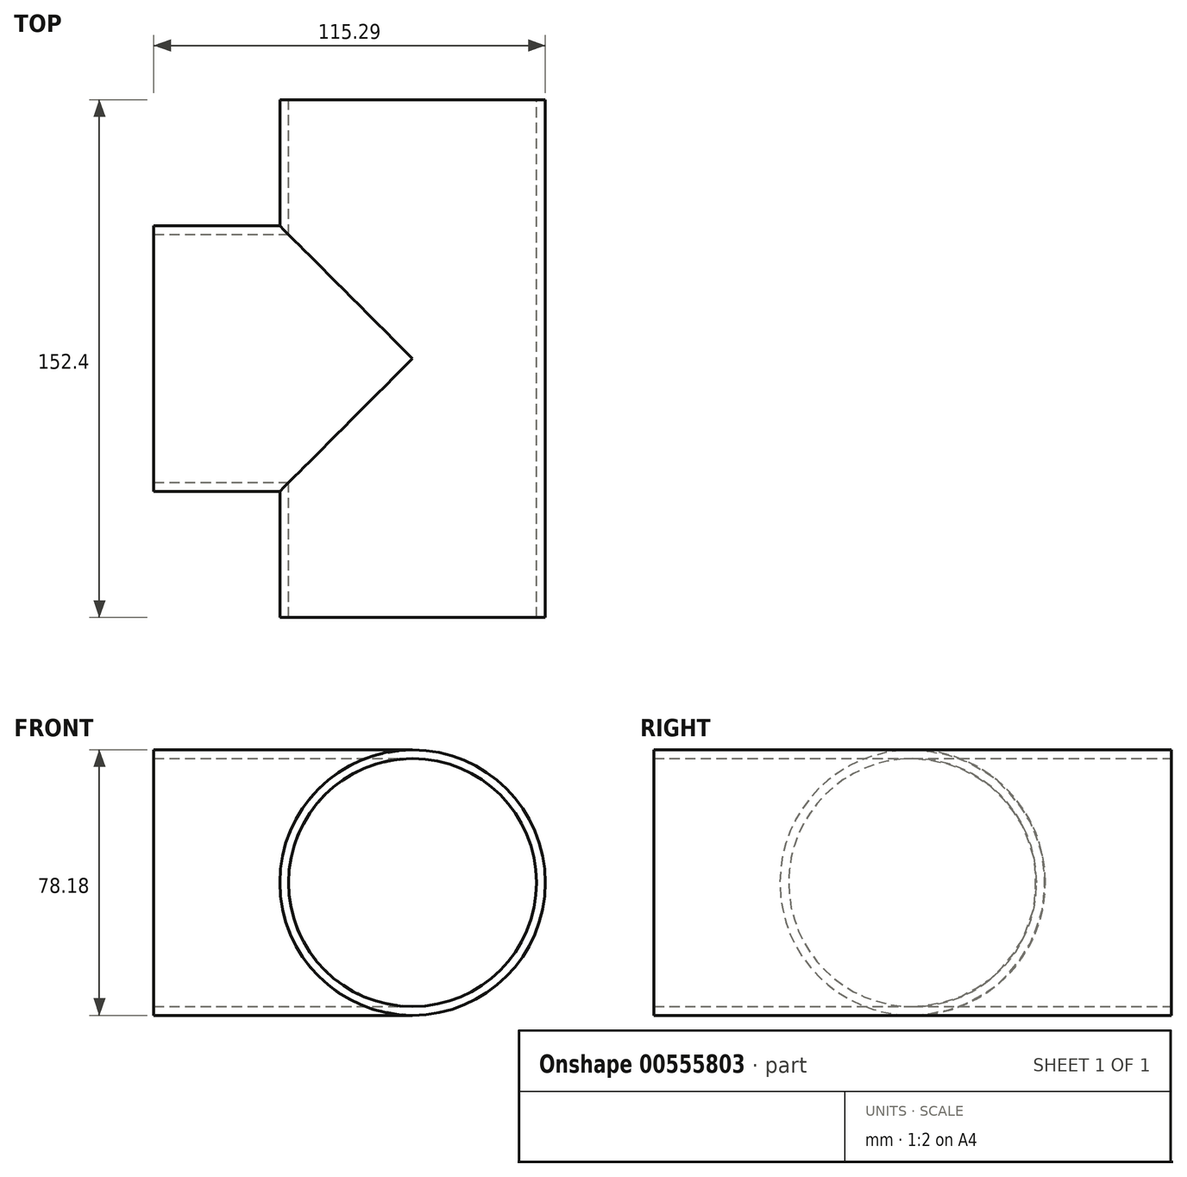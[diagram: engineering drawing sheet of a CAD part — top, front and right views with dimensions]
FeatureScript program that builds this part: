
annotation { "Feature Type Name" : "Feature", "Feature Type Description" : "" }
export const myFeature = defineFeature(function(context is Context, id is Id, definition is map)
    precondition{}
    {
        {
            var Q0;
            Q0=qCreatedBy(makeId("Front.planeOp"),FACE);
            var sketch = newSketch(context, id + "F0", { "sketchPlane" : qUnion([Q0])});
            skCircle(sketch, "E0", {"center": v(0, 0) * mm, "radius": 36.51 * mm});
            skCircle(sketch, "E1", {"center": v(0, 0) * mm, "radius": 39.1 * mm});
            skSolve(sketch);
        }
        {
            var Q0;
            Q0=qCreatedBy(makeId("Right.planeOp"),FACE);
            var sketch = newSketch(context, id + "F1", { "sketchPlane" : qUnion([Q0])});
            skLineSegment(sketch, "E2", {"start": v(0, 0) * mm, "end": v(152.4, 0) * mm});
            skSolve(sketch);
        }
        {
            var Q0;
            Q0=makeQuery(id+"F0.imprint","IMPRINT",FACE,{"disambiguationData":[TD([[makeQuery(id+"F0.imprint","IMPRINT",EDGE,{"derivedFrom":sQuery(id+"F0.wireOp",EDGE,"E0")}),-1.0]])]});
            var Q1;
            Q1=sQuery(id+"F1.wireOp",EDGE,"E2");
            sweep(context, id + "F2", {"profiles" : qUnion([Q0]), "path" : qUnion([Q1])});
        }
        {
            var Q0;
            Q0=qCreatedBy(makeId("Right.planeOp"),FACE);
            var sketch = newSketch(context, id + "F3", { "sketchPlane" : qUnion([Q0])});
            skLineSegment(sketch, "E3.bottom", {"start": v(152.4, -39.1) * mm, "end": v(0, -39.1) * mm, "construction": true});
            skLineSegment(sketch, "E3.left", {"start": v(152.4, -39.1) * mm, "end": v(152.4, 39.1) * mm, "construction": true});
            skPoint(sketch, "E3.middle", {"position": v(0, 0) * mm});
            skLineSegment(sketch, "E4", {"start": v(0, -39.1) * mm, "end": v(0, 39.1) * mm, "construction": true});
            skPoint(sketch, "E3.right.end.orphan", {"position": v(-152.4, 39.1) * mm});
            skPoint(sketch, "E3.right.start.orphan", {"position": v(-152.4, -39.1) * mm});
            skLineSegment(sketch, "E5", {"start": v(0, 0) * mm, "end": v(152.4, 0) * mm, "construction": true});
            skCircle(sketch, "E6", {"center": v(76.2, 0) * mm, "radius": 36.51 * mm});
            skSolve(sketch);
        }
        {
            var Q0;
            Q0 = qSketchRegion(id + "F3", true);
            extrude(context, id + "F4", {"entities" : qUnion([Q0]), "operationType" : NewBodyOperationType.REMOVE, "oppositeDirection" : true, "depth" : 47.5 * mm, "offsetDistance" : 25.4 * mm});
        }
        {
            var Q0;
            Q0=qCreatedBy(makeId("Right.planeOp"),FACE);
            var sketch = newSketch(context, id + "F5", { "sketchPlane" : qUnion([Q0])});
            skLineSegment(sketch, "E7.bottom", {"start": v(152.4, -39.1) * mm, "end": v(0, -39.1) * mm, "construction": true});
            skLineSegment(sketch, "E7.top", {"start": v(152.4, 39.1) * mm, "end": v(0, 39.1) * mm, "construction": true});
            skLineSegment(sketch, "E7.left", {"start": v(152.4, -39.1) * mm, "end": v(152.4, 39.1) * mm, "construction": true});
            skPoint(sketch, "E7.middle", {"position": v(0, 0) * mm});
            skLineSegment(sketch, "E8", {"start": v(0, -39.1) * mm, "end": v(0, 39.1) * mm, "construction": true});
            skPoint(sketch, "E7.right.start.orphan", {"position": v(-152.4, -39.1) * mm});
            skPoint(sketch, "E9.orphan", {"position": v(-152.4, 39.1) * mm});
            skLineSegment(sketch, "E10", {"start": v(0, 0) * mm, "end": v(152.4, 0) * mm, "construction": true});
            skCircle(sketch, "E11", {"center": v(76.2, 0) * mm, "radius": 36.51 * mm});
            skCircle(sketch, "E12", {"center": v(76.2, 0) * mm, "radius": 39.1 * mm});
            skSolve(sketch);
        }
        {
            var Q0;
            Q0 = qSketchRegion(id + "F5", true);
            extrude(context, id + "F6", {"entities" : qUnion([Q0]), "operationType" : NewBodyOperationType.ADD, "oppositeDirection" : true, "depth" : 76.2 * mm, "offsetDistance" : 25.4 * mm});
        }
        {
            var Q0;
            Q0=qCreatedBy(makeId("Front.planeOp"),FACE);
            var sketch = newSketch(context, id + "F7", { "sketchPlane" : qUnion([Q0])});
            skCircle(sketch, "E13", {"center": v(0, 0) * mm, "radius": 36.51 * mm});
            skSolve(sketch);
        }
        {
            var Q0;
            Q0 = qSketchRegion(id + "F7", true);
            extrude(context, id + "F8", {"entities" : qUnion([Q0]), "operationType" : NewBodyOperationType.REMOVE, "oppositeDirection" : true, "depth" : 156.72 * mm, "offsetDistance" : 25.4 * mm});
        }
    });
